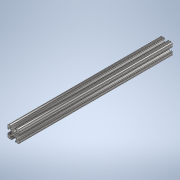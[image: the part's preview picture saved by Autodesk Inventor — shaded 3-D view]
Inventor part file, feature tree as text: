
AUTODESK INVENTOR PART (.ipt)
format: ipt  version: 2020 (Build 240168000, 168)  size: 239,104 bytes
history: native  units: in
note: dims shown in document units (in); Inventor stores cm internally (conversion verified against a paired STEP export)
features: extrude x1, sketch x1
ambient origin geometry x8: Origin, YZ Plane, XZ Plane, XY Plane, X Axis, Y Axis, Z Axis, Center Point
bodies: Solid1 (feature_tree)
feature tree (2):
  extrude  "Extrusion1"  [1 undecoded]
  sketch  "Sketch1"  dims[d0=13.0in d1=0.0in]
note: 1 required parameter value undecoded (feature->parameter linkage not recoverable at this tier; creation-order binding heuristic only, values carry confidence <= 0.55)
